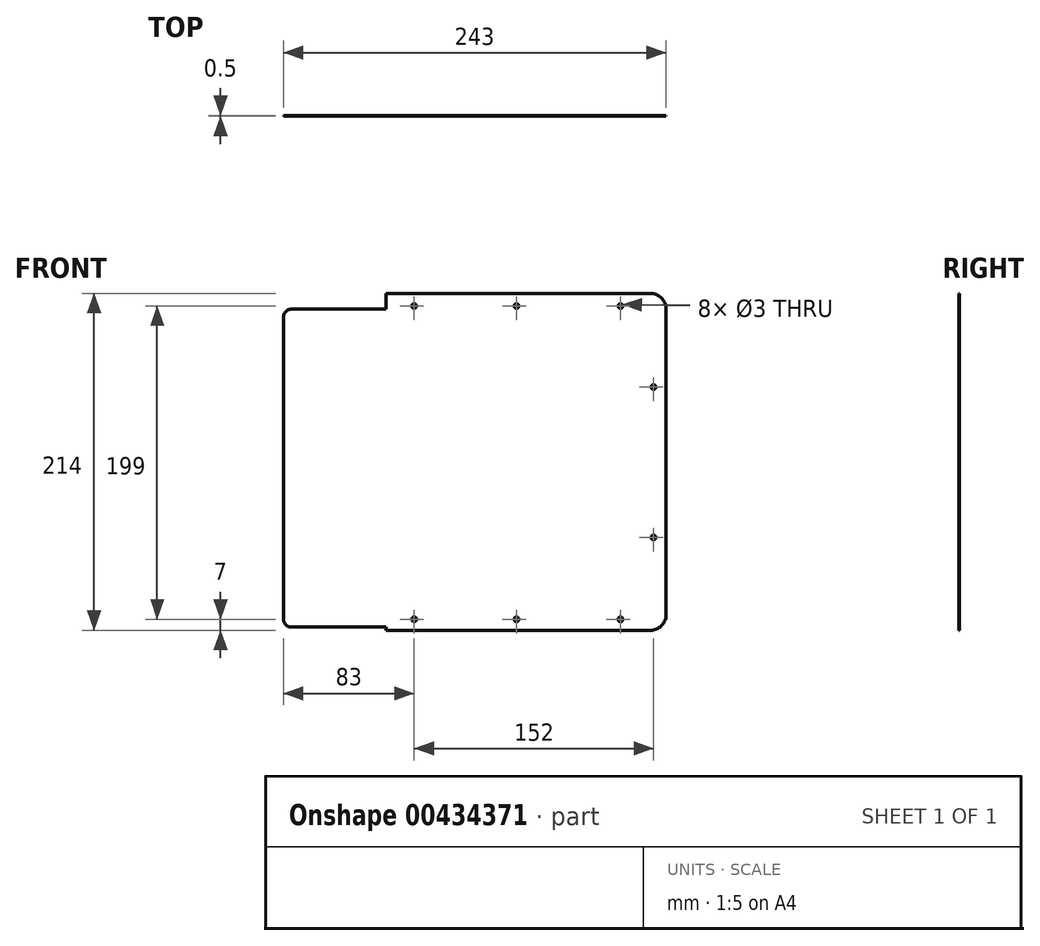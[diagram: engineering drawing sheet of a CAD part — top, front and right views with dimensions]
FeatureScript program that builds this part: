
annotation { "Feature Type Name" : "Feature", "Feature Type Description" : "" }
export const myFeature = defineFeature(function(context is Context, id is Id, definition is map)
    precondition{}
    {
        {
            var Q0;
            Q0=qCreatedBy(makeId("Front.planeOp"),FACE);
            var sketch = newSketch(context, id + "F0", { "sketchPlane" : qUnion([Q0])});
            skLineSegment(sketch, "E0.left", {"start": v(0, 0) * mm, "end": v(0, 214) * mm});
            skLineSegment(sketch, "E0.right", {"start": v(-178, 204) * mm, "end": v(-178, 214) * mm});
            skLineSegment(sketch, "E1.right", {"start": v(-243, 2) * mm, "end": v(-243, 204) * mm});
            skCircle(sketch, "E2", {"center": v(-29, 7) * mm, "radius": 1.5 * mm});
            skCircle(sketch, "E3", {"center": v(-95, 7) * mm, "radius": 1.5 * mm});
            skCircle(sketch, "E4", {"center": v(-160, 7) * mm, "radius": 1.5 * mm});
            skCircle(sketch, "E5", {"center": v(-8, 59) * mm, "radius": 1.5 * mm});
            skCircle(sketch, "E6", {"center": v(-29, 206) * mm, "radius": 1.5 * mm});
            skCircle(sketch, "E7", {"center": v(-95, 206) * mm, "radius": 1.5 * mm});
            skCircle(sketch, "E8", {"center": v(-160, 206) * mm, "radius": 1.5 * mm});
            skLineSegment(sketch, "E9", {"start": v(0, 214) * mm, "end": v(-178, 214) * mm});
            skCircle(sketch, "E10", {"center": v(-8, 154.5) * mm, "radius": 1.5 * mm});
            skLineSegment(sketch, "E11", {"start": v(0, 0) * mm, "end": v(-178, 0) * mm});
            skLineSegment(sketch, "E12", {"start": v(-178, 204) * mm, "end": v(-243, 204) * mm});
            skLineSegment(sketch, "E13", {"start": v(-243, 2) * mm, "end": v(-178, 2) * mm});
            skLineSegment(sketch, "E14", {"start": v(-178, 2) * mm, "end": v(-178, 0) * mm});
            skSolve(sketch);
        }
        {
            var Q0;
            Q0=makeQuery(id+"F0.imprint","IMPRINT",FACE,{"disambiguationData":[TD([[makeQuery(id+"F0.imprint","IMPRINT",EDGE,{"derivedFrom":sQuery(id+"F0.wireOp",EDGE,"E0.left")}),1.0]])]});
            extrude(context, id + "F1", {"entities" : qUnion([Q0]), "depth" : 0.5 * mm, "offsetDistance" : 25 * mm});
        }
        {
            var Q0;
            Q0=makeQuery(id+"F1.opExtrude","SWEPT_EDGE",EDGE,{"disambiguationData":[OSD([sQuery(id+"F0.wireOp",EDGE,"E0.left"),sQuery(id+"F0.wireOp",EDGE,"E9")])]});
            var Q1;
            Q1=makeQuery(id+"F1.opExtrude","SWEPT_EDGE",EDGE,{"disambiguationData":[OSD([sQuery(id+"F0.wireOp",EDGE,"E0.left"),sQuery(id+"F0.wireOp",EDGE,"E11")])]});
            fillet(context, id + "F2", {"entities" : qUnion([Q0, Q1]), "radius" : 10 * mm, "tangentPropagation" : true, "allowEdgeOverflow" : false});
        }
        {
            var Q0;
            Q0=makeQuery(id+"F1.opExtrude","SWEPT_EDGE",EDGE,{"disambiguationData":[OSD([sQuery(id+"F0.wireOp",EDGE,"E1.right"),sQuery(id+"F0.wireOp",EDGE,"E12")])]});
            var Q1;
            Q1=makeQuery(id+"F1.opExtrude","SWEPT_EDGE",EDGE,{"disambiguationData":[OSD([sQuery(id+"F0.wireOp",EDGE,"E1.right"),sQuery(id+"F0.wireOp",EDGE,"E13")])]});
            fillet(context, id + "F3", {"entities" : qUnion([Q0, Q1]), "radius" : 5 * mm, "tangentPropagation" : true, "allowEdgeOverflow" : false});
        }
    });
